# Revit family: Faucet-Tub_and_Shower-Delta-Tesla-17X252_and_14452
name_source: partatom
category: Plumbing Fixtures
revit_build: Autodesk Revit MEP 2012 (Build: 20110916_2132(x64)
units: mm (PartAtom-declared; Revit-internal decimal feet)

## types (3) — shared parameters
Date Modified = January 5, 2015
Default Elevation = 48 "
Depth = 11.715 "
Equipment Abbreviation = TST
Family Version = 1.0
Fixture Flow = 0 GPM
Manufacturer = Delta Faucet Company
Model Disclaimer = Contact Delta Faucet Company for More Information
Product Material = Steel - Delta Faucet Company - Stainless
URL = http://www.deltafaucet.com
Width = 7.65 "
zz Angle 1 = 220.000°
zz Integer 2 = 3
zz Length 1 = 7 "
zz Length 4 = 7 "
zz YesNo 1 = Yes
zz YesNo 2 = Yes

## per-type parameters (varying)
| type | Description | Model | zz Integer 1 | zz Length 6 |
| 17 Series | Tesla Tub and Shower Faucet Trim, Series 17 | 17T252 | 1 | 5 " |
| 17 Series, Thermostatic | Tesla Tub and Shower Faucet Trim with TempAssure Thermostatic | 17252 | 2 | 5 " |
| 14 Series | Tesla Tub and Shower Faucet Trim, Series 14 | 14452 | 3 | 0 " |

## geometry (parser evidence)
native form markers: Blend x2, Sweep x1
no freeform markers — native parametric forms only
